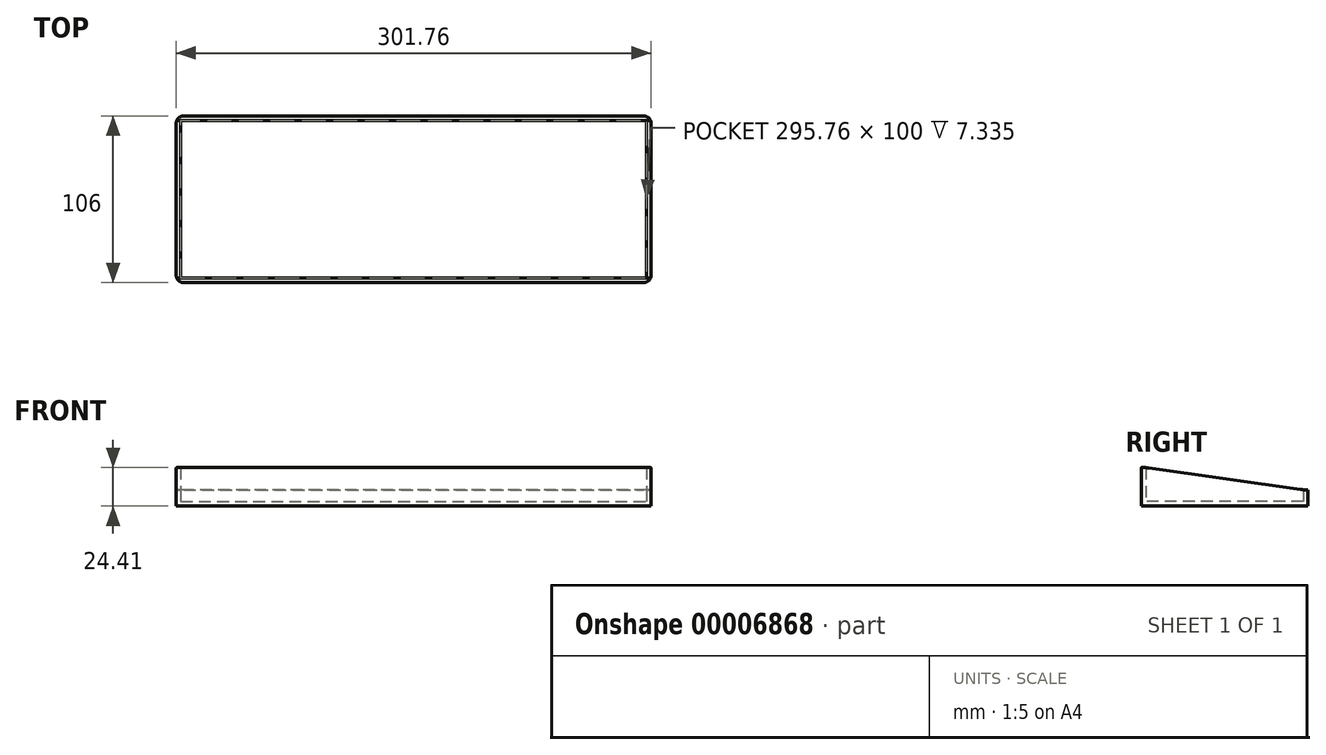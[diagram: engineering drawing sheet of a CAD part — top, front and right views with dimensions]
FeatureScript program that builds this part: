
annotation { "Feature Type Name" : "Feature", "Feature Type Description" : "" }
export const myFeature = defineFeature(function(context is Context, id is Id, definition is map)
    precondition{}
    {
        {
            var Q0;
            Q0=qCreatedBy(makeId("Top.planeOp"),FACE);
            var sketch = newSketch(context, id + "F0", { "sketchPlane" : qUnion([Q0])});
            skLineSegment(sketch, "E0.bottom", {"start": v(-67.03, 105.94) * mm, "end": v(228.73, 105.94) * mm});
            skLineSegment(sketch, "E0.top", {"start": v(-67.03, 5.94) * mm, "end": v(228.73, 5.94) * mm});
            skLineSegment(sketch, "E0.left", {"start": v(-67.03, 105.94) * mm, "end": v(-67.03, 5.94) * mm});
            skLineSegment(sketch, "E0.right", {"start": v(228.73, 105.94) * mm, "end": v(228.73, 5.94) * mm});
            skLineSegment(sketch, "E1.0", {"start": v(-70.03, 108.94) * mm, "end": v(231.73, 108.94) * mm});
            skLineSegment(sketch, "E1.1", {"start": v(-70.03, 108.94) * mm, "end": v(-70.03, 2.94) * mm});
            skLineSegment(sketch, "E1.2", {"start": v(-70.03, 2.94) * mm, "end": v(231.73, 2.94) * mm});
            skLineSegment(sketch, "E1.3", {"start": v(231.73, 108.94) * mm, "end": v(231.73, 2.94) * mm});
            skLineSegment(sketch, "E2", {"start": v(228.73, 105.94) * mm, "end": v(231.73, 105.94) * mm});
            skLineSegment(sketch, "E3", {"start": v(228.73, 5.94) * mm, "end": v(231.73, 5.94) * mm});
            skLineSegment(sketch, "E4", {"start": v(-67.03, 5.94) * mm, "end": v(-70.03, 5.94) * mm});
            skLineSegment(sketch, "E5", {"start": v(-67.03, 105.94) * mm, "end": v(-70.03, 105.94) * mm});
            skLineSegment(sketch, "E6.0", {"start": v(-64.03, 102.94) * mm, "end": v(225.73, 102.94) * mm});
            skLineSegment(sketch, "E6.1", {"start": v(-64.03, 102.94) * mm, "end": v(-64.03, 8.94) * mm});
            skLineSegment(sketch, "E6.2", {"start": v(-64.03, 8.94) * mm, "end": v(225.73, 8.94) * mm});
            skLineSegment(sketch, "E6.3", {"start": v(225.73, 102.94) * mm, "end": v(225.73, 8.94) * mm});
            skLineSegment(sketch, "E7", {"start": v(-64.03, 102.94) * mm, "end": v(-67.03, 102.94) * mm});
            skLineSegment(sketch, "E8", {"start": v(225.73, 102.94) * mm, "end": v(228.73, 102.94) * mm});
            skLineSegment(sketch, "E9", {"start": v(225.73, 8.94) * mm, "end": v(228.73, 8.94) * mm});
            skLineSegment(sketch, "E10", {"start": v(-64.03, 8.94) * mm, "end": v(-67.03, 8.94) * mm});
            skLineSegment(sketch, "E11", {"start": v(-64.03, 102.94) * mm, "end": v(-64.03, 105.94) * mm});
            skLineSegment(sketch, "E12", {"start": v(225.73, 102.94) * mm, "end": v(225.73, 105.94) * mm});
            skLineSegment(sketch, "E13", {"start": v(225.73, 8.94) * mm, "end": v(225.73, 5.94) * mm});
            skLineSegment(sketch, "E14", {"start": v(-64.03, 8.94) * mm, "end": v(-64.03, 5.94) * mm});
            skSolve(sketch);
        }
        {
            var Q0;
            Q0=makeQuery(id+"F0.imprint","IMPRINT",FACE,{"disambiguationData":[TD([[makeQuery(id+"F0.imprint","IMPRINT",EDGE,{"derivedFrom":sQuery(id+"F0.wireOp",EDGE,"E6.0")}),-1.0]])]});
            var Q1;
            Q1=makeQuery(id+"F0.imprint","IMPRINT",FACE,{"disambiguationData":[TD([[makeQuery(id+"F0.imprint","IMPRINT",EDGE,{"derivedFrom":sQuery(id+"F0.wireOp",EDGE,"E6.1")}),-1.0]])]});
            var Q2;
            {var subQ4=sQuery(id+"F0.wireOp",EDGE,"E10");Q2=makeQuery(id+"F0.imprint","IMPRINT",FACE,{"disambiguationData":[TD([[makeQuery(id+"F0.imprint","IMPRINT",EDGE,{"derivedFrom":subQ4}),1.0]])]});}
            var Q3;
            Q3=makeQuery(id+"F0.imprint","IMPRINT",FACE,{"disambiguationData":[TD([[makeQuery(id+"F0.imprint","IMPRINT",EDGE,{"derivedFrom":sQuery(id+"F0.wireOp",EDGE,"E6.2")}),-1.0]])]});
            var Q4;
            {var subQ4=sQuery(id+"F0.wireOp",EDGE,"E9");Q4=makeQuery(id+"F0.imprint","IMPRINT",FACE,{"disambiguationData":[TD([[makeQuery(id+"F0.imprint","IMPRINT",EDGE,{"derivedFrom":subQ4}),-1.0]])]});}
            var Q5;
            Q5=makeQuery(id+"F0.imprint","IMPRINT",FACE,{"disambiguationData":[TD([[makeQuery(id+"F0.imprint","IMPRINT",EDGE,{"derivedFrom":sQuery(id+"F0.wireOp",EDGE,"E6.3")}),1.0]])]});
            var Q6;
            {var subQ4=sQuery(id+"F0.wireOp",EDGE,"E8");Q6=makeQuery(id+"F0.imprint","IMPRINT",FACE,{"disambiguationData":[TD([[makeQuery(id+"F0.imprint","IMPRINT",EDGE,{"derivedFrom":subQ4}),1.0]])]});}
            var Q7;
            Q7=makeQuery(id+"F0.imprint","IMPRINT",FACE,{"disambiguationData":[TD([[makeQuery(id+"F0.imprint","IMPRINT",EDGE,{"derivedFrom":sQuery(id+"F0.wireOp",EDGE,"E6.0")}),1.0]])]});
            var Q8;
            {var subQ4=sQuery(id+"F0.wireOp",EDGE,"E7");Q8=makeQuery(id+"F0.imprint","IMPRINT",FACE,{"disambiguationData":[TD([[makeQuery(id+"F0.imprint","IMPRINT",EDGE,{"derivedFrom":subQ4}),-1.0]])]});}
            extrude(context, id + "F1", {"entities" : qUnion([Q0, Q1, Q2, Q3, Q4, Q5, Q6, Q7, Q8]), "depth" : 3 * mm});
        }
        {
            var Q0;
            Q0=makeQuery(id+"F0.imprint","IMPRINT",FACE,{"disambiguationData":[TD([[makeQuery(id+"F0.imprint","IMPRINT",EDGE,{"derivedFrom":sQuery(id+"F0.wireOp",EDGE,"E0.left")}),-1.0]])]});
            var Q1;
            Q1=makeQuery(id+"F0.imprint","IMPRINT",FACE,{"disambiguationData":[TD([[makeQuery(id+"F0.imprint","IMPRINT",EDGE,{"derivedFrom":sQuery(id+"F0.wireOp",EDGE,"E0.right")}),1.0]])]});
            extrude(context, id + "F2", {"entities" : qUnion([Q0, Q1]), "operationType" : NewBodyOperationType.ADD, "depth" : 25 * mm});
        }
        {
            var Q0;
            Q0=makeQuery(id+"F2.opExtrude","SWEPT_FACE",FACE,{"disambiguationData":[OSD([sQuery(id+"F0.wireOp",EDGE,"E0.left")])]});
            var sketch = newSketch(context, id + "F3", { "sketchPlane" : qUnion([Q0])});
            skLineSegment(sketch, "E15", {"start": v(1.73, 25) * mm, "end": v(105.94, 10.35) * mm});
            skSolve(sketch);
        }
        {
            var Q0;
            {var subQ0=sQuery(id+"F3.wireOp",EDGE,"E15");Q0=makeQuery(id+"F3.imprint","IMPRINT",FACE,{"disambiguationData":[TD([[makeQuery(id+"F3.imprint","IMPRINT",EDGE,{"derivedFrom":subQ0}),1.0]])]});}
            extrude(context, id + "F4", {"entities" : qUnion([Q0]), "operationType" : NewBodyOperationType.REMOVE, "endBound" : BoundingType.THROUGH_ALL, "oppositeDirection" : true, "depth" : 25 * mm, "hasSecondDirection" : true, "secondDirectionBound" : SecondDirectionBoundingType.THROUGH_ALL, "secondDirectionOppositeDirection" : false, "secondDirectionDepth" : 25 * mm});
        }
        {
            var Q0;
            Q0=makeQuery(id+"F0.imprint","IMPRINT",FACE,{"disambiguationData":[TD([[makeQuery(id+"F0.imprint","IMPRINT",EDGE,{"derivedFrom":sQuery(id+"F0.wireOp",EDGE,"E0.bottom")}),1.0]])]});
            extrude(context, id + "F5", {"entities" : qUnion([Q0]), "operationType" : NewBodyOperationType.ADD, "depth" : 10.34 * mm});
        }
        {
            var Q0;
            Q0=makeQuery(id+"F0.imprint","IMPRINT",FACE,{"disambiguationData":[TD([[makeQuery(id+"F0.imprint","IMPRINT",EDGE,{"derivedFrom":sQuery(id+"F0.wireOp",EDGE,"E0.top")}),-1.0]])]});
            extrude(context, id + "F6", {"entities" : qUnion([Q0]), "operationType" : NewBodyOperationType.ADD, "depth" : 24.4 * mm});
        }
        {
            var Q0;
            Q0=makeQuery(id+"F1.opExtrude","CAP_EDGE",EDGE,{"disambiguationData":[OSD([sQuery(id+"F0.wireOp",EDGE,"E0.bottom")])],"isStart":false});
            var Q1;
            Q1=makeQuery(id+"F1.opExtrude","CAP_EDGE",EDGE,{"disambiguationData":[OSD([sQuery(id+"F0.wireOp",EDGE,"E0.right")])],"isStart":false});
            var Q2;
            Q2=makeQuery(id+"F1.opExtrude","CAP_EDGE",EDGE,{"disambiguationData":[OSD([sQuery(id+"F0.wireOp",EDGE,"E0.top")])],"isStart":false});
            var Q3;
            Q3=makeQuery(id+"F1.opExtrude","CAP_EDGE",EDGE,{"disambiguationData":[OSD([sQuery(id+"F0.wireOp",EDGE,"E0.left")])],"isStart":false});
            var Q4;
            Q4=makeQuery(id+"F5.opExtrude","SWEPT_EDGE",EDGE,{"disambiguationData":[OSD([sQuery(id+"F0.wireOp",EDGE,"E1.0"),sQuery(id+"F0.wireOp",EDGE,"E1.3")])]});
            var Q5;
            Q5=makeQuery(id+"F6.opExtrude","SWEPT_EDGE",EDGE,{"disambiguationData":[OSD([sQuery(id+"F0.wireOp",EDGE,"E1.2"),sQuery(id+"F0.wireOp",EDGE,"E1.3")])]});
            var Q6;
            Q6=makeQuery(id+"F6.opExtrude","SWEPT_EDGE",EDGE,{"disambiguationData":[OSD([sQuery(id+"F0.wireOp",EDGE,"E1.1"),sQuery(id+"F0.wireOp",EDGE,"E1.2")])]});
            var Q7;
            Q7=makeQuery(id+"F5.opExtrude","SWEPT_EDGE",EDGE,{"disambiguationData":[OSD([sQuery(id+"F0.wireOp",EDGE,"E1.0"),sQuery(id+"F0.wireOp",EDGE,"E1.1")])]});
            fillet(context, id + "F7", {"entities" : qUnion([Q0, Q1, Q2, Q3, Q4, Q5, Q6, Q7]), "radius" : 5 * mm, "tangentPropagation" : true, "allowEdgeOverflow" : false});
        }
    });
